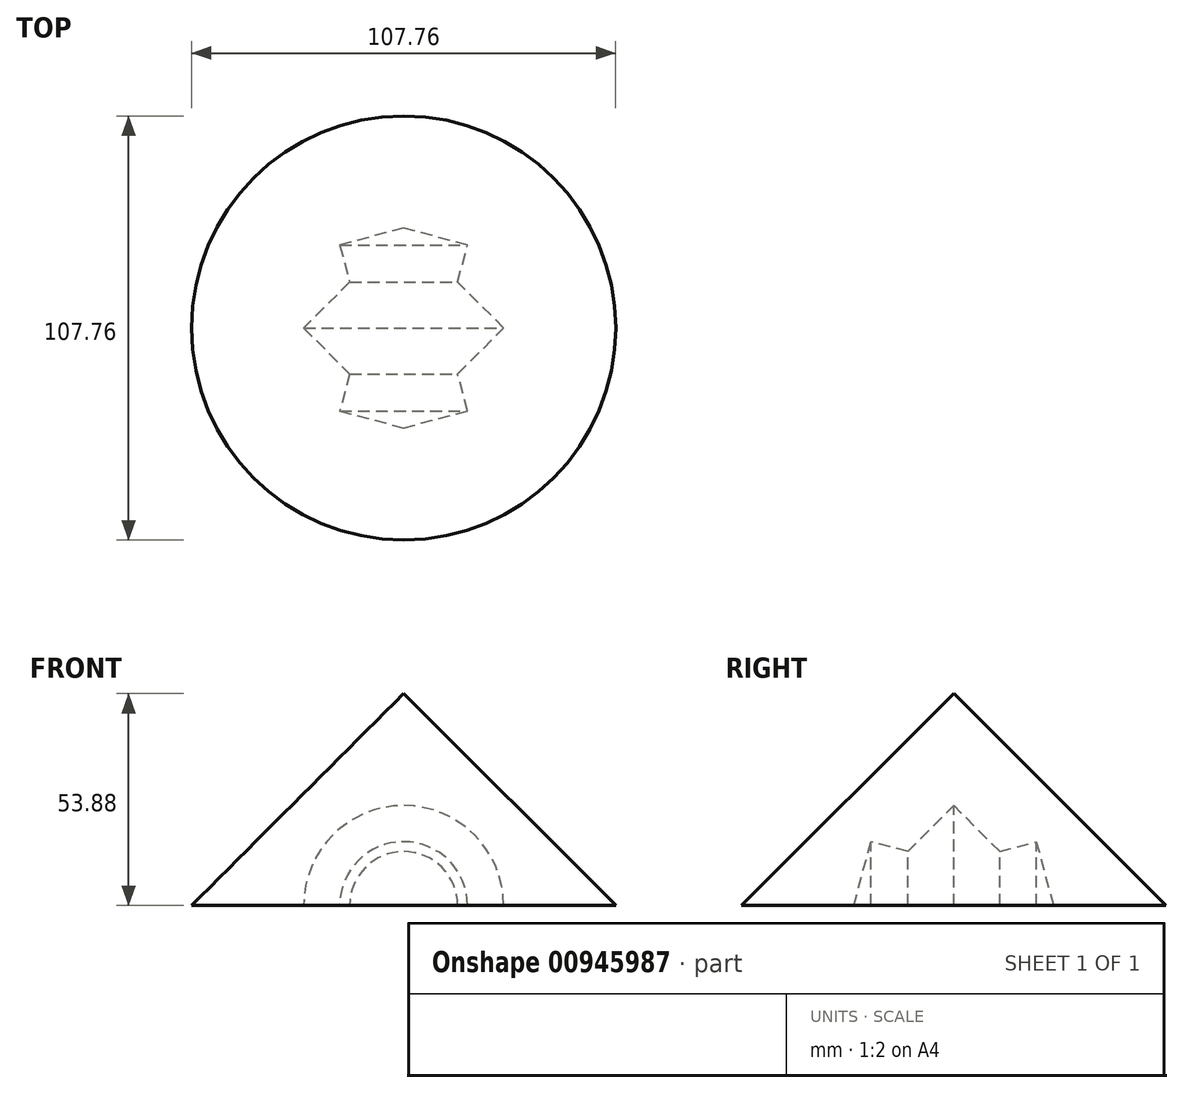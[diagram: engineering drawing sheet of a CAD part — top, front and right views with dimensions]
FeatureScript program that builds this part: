
annotation { "Feature Type Name" : "Feature", "Feature Type Description" : "" }
export const myFeature = defineFeature(function(context is Context, id is Id, definition is map)
    precondition{}
    {
        {
            var Q0;
            Q0=qCreatedBy(makeId("Front.planeOp"),FACE);
            var sketch = newSketch(context, id + "F0", { "sketchPlane" : qUnion([Q0])});
            skLineSegment(sketch, "E0", {"start": v(0, 53.88) * mm, "end": v(0, 0) * mm});
            skLineSegment(sketch, "E1", {"start": v(0, 0) * mm, "end": v(53.88, 0) * mm});
            skLineSegment(sketch, "E2", {"start": v(53.88, 0) * mm, "end": v(0, 53.88) * mm});
            skSolve(sketch);
        }
        {
            var Q0;
            Q0=makeQuery(id+"F0.imprint","IMPRINT",FACE,{"disambiguationData":[TD([[makeQuery(id+"F0.imprint","IMPRINT",EDGE,{"derivedFrom":sQuery(id+"F0.wireOp",EDGE,"E0")}),1.0]])]});
            var Q1;
            Q1=sQuery(id+"F0.wireOp",EDGE,"E0");
            revolve(context, id + "F1", {"surfaceOperationType" : NewSurfaceOperationType.NEW, "entities" : qUnion([Q0]), "axis" : qUnion([Q1]), "revolveType" : RevolveType.FULL});
        }
        {
            var Q0;
            Q0=qCreatedBy(makeId("Top.planeOp"),FACE);
            var sketch = newSketch(context, id + "F2", { "sketchPlane" : qUnion([Q0])});
            skLineSegment(sketch, "E3", {"start": v(0, 0) * mm, "end": v(0, 25.4) * mm});
            skLineSegment(sketch, "E4", {"start": v(0, 25.4) * mm, "end": v(16.24, 21.05) * mm});
            skLineSegment(sketch, "E5", {"start": v(16.24, 21.05) * mm, "end": v(13.73, 11.67) * mm});
            skLineSegment(sketch, "E6", {"start": v(13.73, 11.67) * mm, "end": v(25.4, 0) * mm});
            skLineSegment(sketch, "E7", {"start": v(25.4, 0) * mm, "end": v(0, 0) * mm, "construction": true});
            skLineSegment(sketch, "E8.MirrorCS", {"start": v(0, 0) * mm, "end": v(0, -25.4) * mm});
            skLineSegment(sketch, "E9.MirrorCS", {"start": v(0, -25.4) * mm, "end": v(16.24, -21.05) * mm});
            skLineSegment(sketch, "E10.MirrorCS", {"start": v(16.24, -21.05) * mm, "end": v(13.73, -11.67) * mm});
            skLineSegment(sketch, "E11.MirrorCS", {"start": v(13.73, -11.67) * mm, "end": v(25.4, 0) * mm});
            skSolve(sketch);
        }
        {
            var Q0;
            Q0 = qSketchRegion(id + "F2", true);
            var Q1;
            Q1=sQuery(id+"F2.wireOp",EDGE,"E8.MirrorCS");
            revolve(context, id + "F3", {"surfaceOperationType" : NewSurfaceOperationType.NEW, "entities" : qUnion([Q0]), "axis" : qUnion([Q1]), "revolveType" : RevolveType.FULL});
        }
        {
            var Q0;
            Q0=makeQuery(id+"F3.opRevolve","SWEPT_BODY",BODY,{"disambiguationData":[OSD([sQuery(id+"F2.wireOp",EDGE,"E3"),sQuery(id+"F2.wireOp",EDGE,"E4"),sQuery(id+"F2.wireOp",EDGE,"E5"),sQuery(id+"F2.wireOp",EDGE,"E6"),sQuery(id+"F2.wireOp",EDGE,"E8.MirrorCS"),sQuery(id+"F2.wireOp",EDGE,"E9.MirrorCS"),sQuery(id+"F2.wireOp",EDGE,"E10.MirrorCS"),sQuery(id+"F2.wireOp",EDGE,"E11.MirrorCS")])]});
            var Q1;
            Q1=makeQuery(id+"F1.opRevolve","SWEPT_BODY",BODY,{"disambiguationData":[OSD([sQuery(id+"F0.wireOp",EDGE,"E0"),sQuery(id+"F0.wireOp",EDGE,"E1"),sQuery(id+"F0.wireOp",EDGE,"E2")])]});
            booleanBodies(context, id + "F4", {"operationType" : BooleanOperationType.SUBTRACTION, "tools" : qUnion([Q0]), "targets" : qUnion([Q1])});
        }
    });
